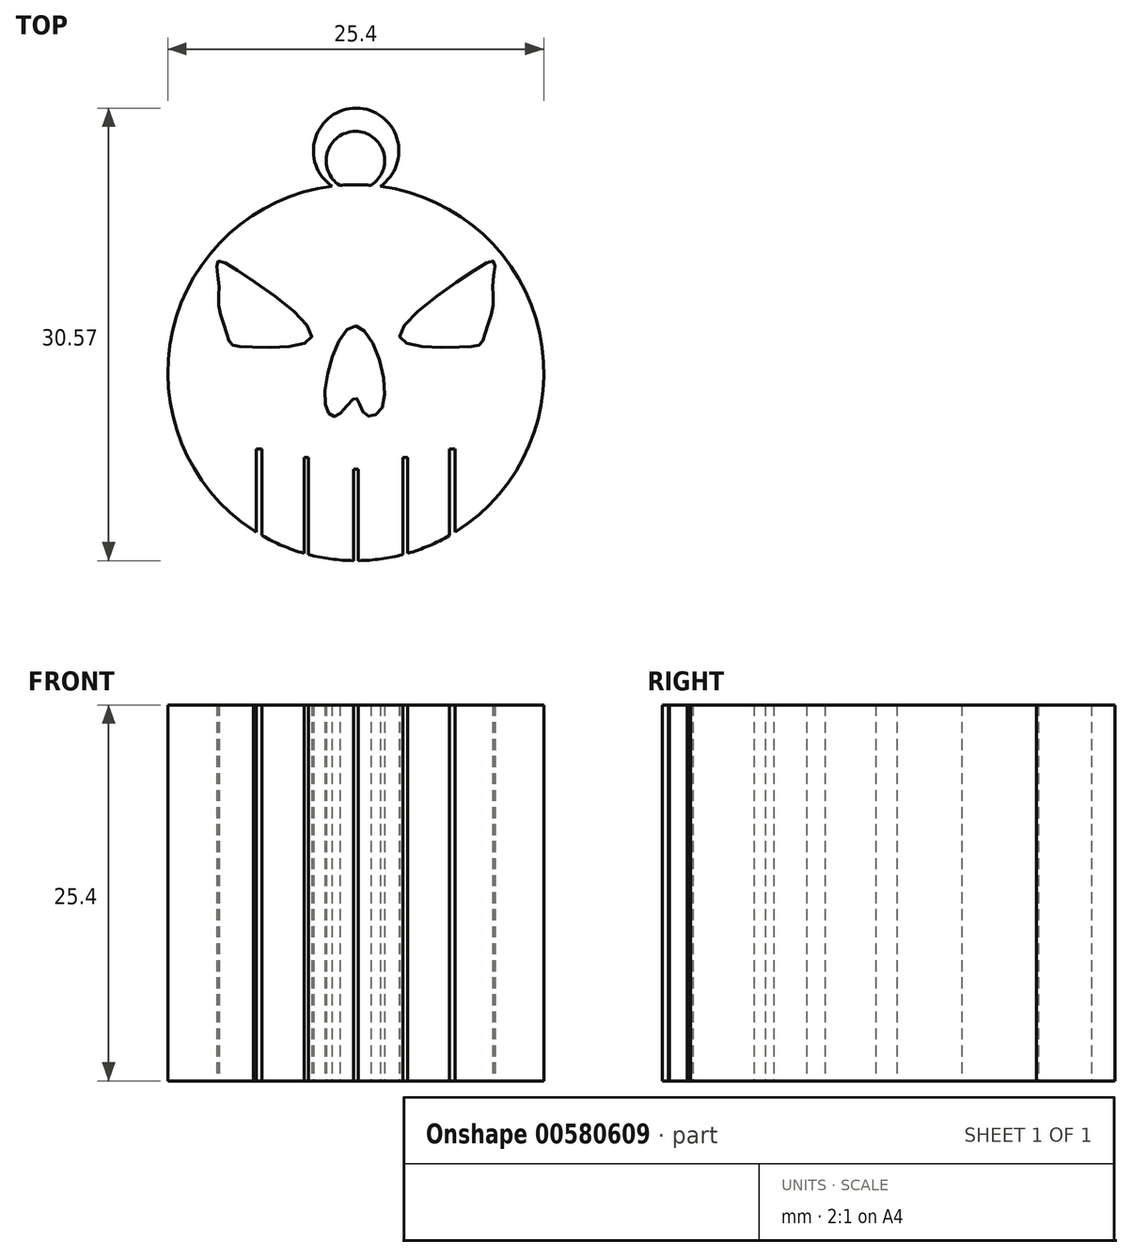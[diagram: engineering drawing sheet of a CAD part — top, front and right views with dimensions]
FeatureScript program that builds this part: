
annotation { "Feature Type Name" : "Feature", "Feature Type Description" : "" }
export const myFeature = defineFeature(function(context is Context, id is Id, definition is map)
    precondition{}
    {
        {
            var Q0;
            Q0=qCreatedBy(makeId("Top.planeOp"),FACE);
            var sketch = newSketch(context, id + "F0", { "sketchPlane" : qUnion([Q0])});
            skCircle(sketch, "E0", {"center": v(0, 9.82) * mm, "radius": 12.7 * mm});
            skLineSegment(sketch, "E1.top", {"start": v(-6.93, -0.83) * mm, "end": v(-6.88, -0.83) * mm});
            skPoint(sketch, "E2.visualSharp", {"position": v(-12.39, 3.12) * mm});
            skPoint(sketch, "E3.visualSharp", {"position": v(12.43, 3.12) * mm});
            skPoint(sketch, "E4.visualSharp", {"position": v(12.43, -0.83) * mm});
            skPoint(sketch, "E5.visualSharp", {"position": v(-12.39, -0.83) * mm});
            skLineSegment(sketch, "E6.right", {"start": v(-6.88, -0.83) * mm, "end": v(-6.88, -0.86) * mm});
            skPoint(sketch, "E6.middle", {"position": v(0.02, -4.35) * mm});
            skPoint(sketch, "E6.middle.positionSnap0", {"position": v(0.02, -0.83) * mm});
            skPoint(sketch, "E6.centerSnap0", {"position": v(0.02, -0.83) * mm});
            skPoint(sketch, "E7.visualSharp", {"position": v(-6.88, -7.88) * mm});
            skPoint(sketch, "E8.visualSharp", {"position": v(6.93, -7.88) * mm});
            skFitSpline(sketch, "E9", {"points": [v(0, 12.97) * mm, v(-2.1, 7.95) * mm, v(-1.27, 6.91) * mm, v(0, 8.11) * mm, v(0.58, 7.02) * mm, v(1.84, 7.62) * mm, v(0, 12.97) * mm]});
            skFitSpline(sketch, "E10", {"points": [v(8, 16.73) * mm, v(2.98, 12.2) * mm, v(7.07, 11.55) * mm, v(8.44, 11.77) * mm, v(8.77, 12.59) * mm, v(9.26, 14.28) * mm, v(9.26, 15.86) * mm, v(9.37, 17.28) * mm, v(8, 16.73) * mm]});
            skFitSpline(sketch, "E11.MirrorC", {"points": [v(-8, 16.73) * mm, v(-2.98, 12.2) * mm, v(-7.07, 11.55) * mm, v(-8.44, 11.77) * mm, v(-8.77, 12.59) * mm, v(-9.26, 14.28) * mm, v(-9.26, 15.86) * mm, v(-9.37, 17.28) * mm, v(-8, 16.73) * mm]});
            skPoint(sketch, "E5.filletArc.end.orphan", {"position": v(-11, -0.83) * mm});
            skPoint(sketch, "E12.orphan", {"position": v(11.05, -0.83) * mm});
            skPoint(sketch, "E6.left.start.orphan", {"position": v(6.93, -0.83) * mm});
            skPoint(sketch, "E13.orphan", {"position": v(5.55, -7.88) * mm});
            skPoint(sketch, "E14.top.end.orphan", {"position": v(4.92, -1.89) * mm});
            skPoint(sketch, "E15.bottom.start.orphan", {"position": v(0.02, -7.88) * mm});
            skPoint(sketch, "E7.filletArc.end.orphan", {"position": v(-5.5, -7.88) * mm});
            skPoint(sketch, "E16.top.end.orphan", {"position": v(-4.92, -1.89) * mm});
            skLineSegment(sketch, "E17.bottom", {"start": v(-0.14, -2.88) * mm, "end": v(0.15, -2.88) * mm});
            skLineSegment(sketch, "E17.top", {"start": v(-0.14, 3.3) * mm, "end": v(0.15, 3.3) * mm});
            skLineSegment(sketch, "E17.left", {"start": v(-0.14, -2.88) * mm, "end": v(-0.14, 3.3) * mm});
            skLineSegment(sketch, "E17.right", {"start": v(0.15, -2.88) * mm, "end": v(0.15, 3.3) * mm});
            skLineSegment(sketch, "E18.bottom", {"start": v(3.19, -2.48) * mm, "end": v(3.5, -2.48) * mm});
            skLineSegment(sketch, "E18.top", {"start": v(3.19, 4.09) * mm, "end": v(3.5, 4.09) * mm});
            skLineSegment(sketch, "E18.left", {"start": v(3.19, -2.48) * mm, "end": v(3.19, 4.09) * mm});
            skLineSegment(sketch, "E18.right", {"start": v(3.5, -2.48) * mm, "end": v(3.5, 4.09) * mm});
            skLineSegment(sketch, "E19.MirrorCS", {"start": v(-3.19, -2.48) * mm, "end": v(-3.19, 4.09) * mm});
            skLineSegment(sketch, "E20.MirrorCS", {"start": v(-3.5, -2.48) * mm, "end": v(-3.5, 4.09) * mm});
            skLineSegment(sketch, "E21.MirrorCS", {"start": v(-3.19, 4.09) * mm, "end": v(-3.5, 4.09) * mm});
            skLineSegment(sketch, "E22.MirrorCS", {"start": v(-3.19, -2.48) * mm, "end": v(-3.5, -2.48) * mm});
            skLineSegment(sketch, "E23.bottom", {"start": v(6.33, -1.2) * mm, "end": v(6.72, -1.2) * mm});
            skLineSegment(sketch, "E23.top", {"start": v(6.33, 4.66) * mm, "end": v(6.72, 4.66) * mm});
            skLineSegment(sketch, "E23.left", {"start": v(6.33, -1.2) * mm, "end": v(6.33, 4.66) * mm});
            skLineSegment(sketch, "E23.right", {"start": v(6.72, -1.2) * mm, "end": v(6.72, 4.66) * mm});
            skLineSegment(sketch, "E24.MirrorCS", {"start": v(-6.33, -1.2) * mm, "end": v(-6.33, 4.66) * mm});
            skLineSegment(sketch, "E25.MirrorCS", {"start": v(-6.72, -1.2) * mm, "end": v(-6.72, 4.66) * mm});
            skLineSegment(sketch, "E26.MirrorCS", {"start": v(-6.33, 4.66) * mm, "end": v(-6.72, 4.66) * mm});
            skLineSegment(sketch, "E27.MirrorCS", {"start": v(-6.33, -1.2) * mm, "end": v(-6.72, -1.2) * mm});
            skArc(sketch, "E28", {"start": v(1.65, 22.41) * mm, "mid": v(0.03, 27.69) * mm, "end": v(-1.6, 22.42) * mm});
            skArc(sketch, "E29", {"start": v(1.03, 22.48) * mm, "mid": v(-0.04, 26.12) * mm, "end": v(-1.09, 22.47) * mm});
            skSolve(sketch);
        }
        {
            var Q0;
            {var subQ18=sQuery(id+"F0.wireOp",EDGE,"E1.top");Q0=makeQuery(id+"F0.imprint","IMPRINT",FACE,{"disambiguationData":[TD([[makeQuery(id+"F0.imprint","IMPRINT",EDGE,{"derivedFrom":subQ18}),1.0]])]});}
            var Q1;
            {var subQ0=sQuery(id+"F0.wireOp",EDGE,"E28");Q1=makeQuery(id+"F0.imprint","IMPRINT",FACE,{"disambiguationData":[TD([[makeQuery(id+"F0.imprint","IMPRINT",EDGE,{"derivedFrom":subQ0}),1.0]])]});}
            extrude(context, id + "F1", {"entities" : qUnion([Q0, Q1]), "depth" : 25.4 * mm, "offsetDistance" : 25.4 * mm});
        }
    });
